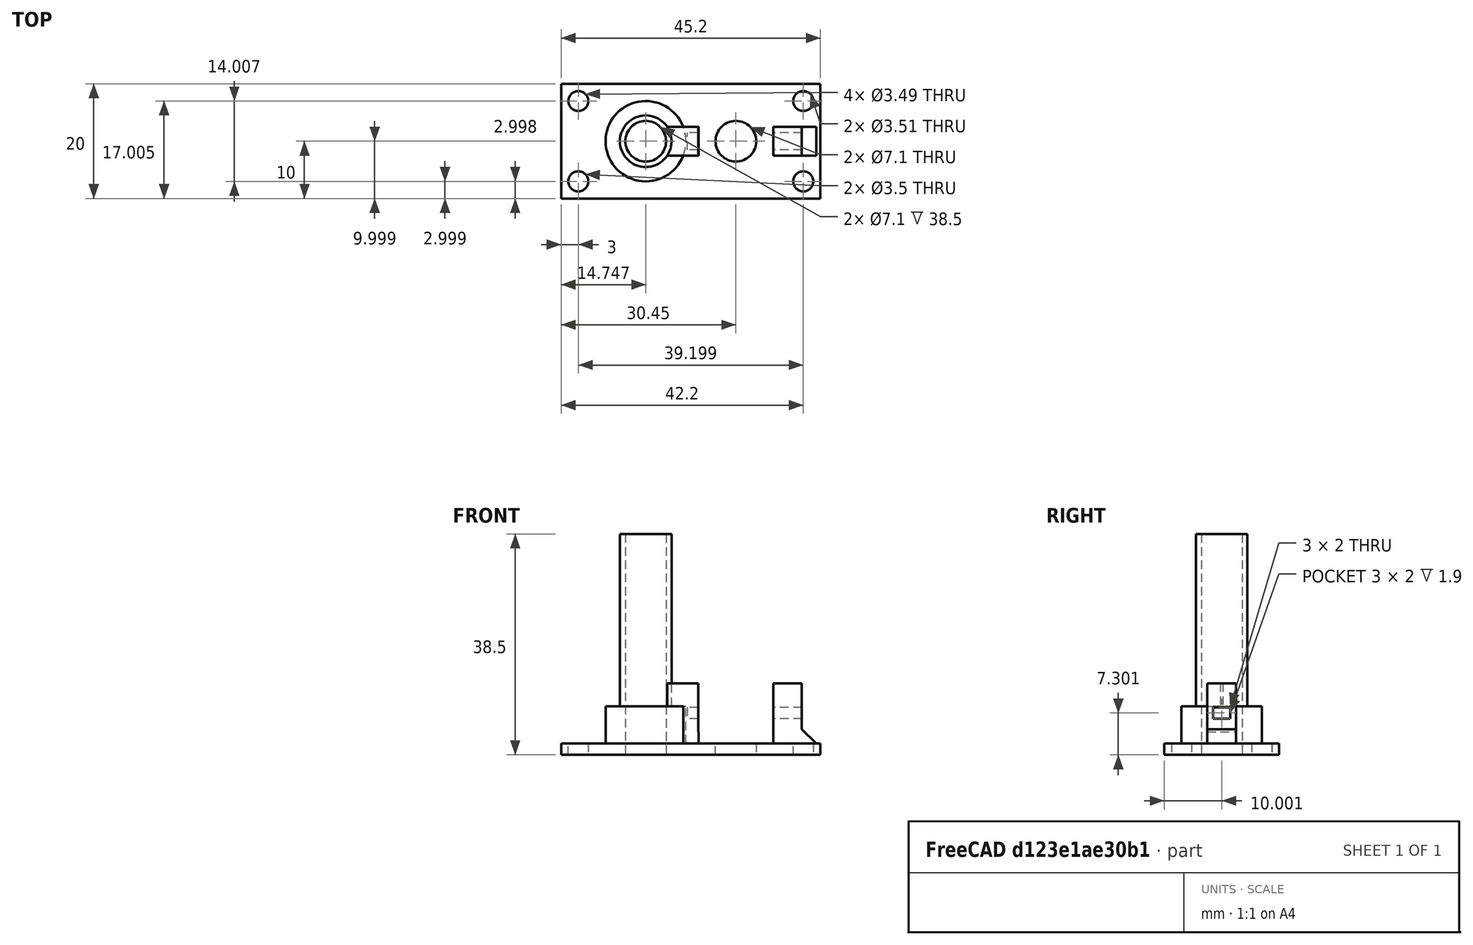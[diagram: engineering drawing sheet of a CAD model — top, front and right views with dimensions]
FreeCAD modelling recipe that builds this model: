
FCSTD DOCUMENT  (FreeCAD 0.17R13522 (Git))
Label: base_media_con_soportes_v3
License: CreativeCommons Attribution-ShareAlike
LicenseURL: http://creativecommons.org/licenses/by-sa/4.0/
objects: Part::Extrusion×15, Part::Part2DObjectPython×13, Part::Cut×13, Part::Fuse×10, Part::Feature×5, Part::Box×2, Part::MultiFuse×1, Part::Chamfer×1
note: 60 computed .brp shape members not serialized (recipe doc carries the construction recipe); baked Part::Feature solids carry a one-line shape summary decoded from their .brp

FEATURE [Part::Box] Box  label="placa base"
  AttacherType = Attacher::AttachEngine3D
  Height = 2
  Length = 45.2
  Width = 20
FEATURE [Part::Part2DObjectPython] Circle  label="taladro inferior izquierdo"  # Draft 2D object (typed FeaturePython)
  FirstAngle = 0
  LastAngle = 0
  MakeFace = false
  Placement = pos=(3,2.99873,2) rot=(0,0,1;3.14159rad)
  Radius = 1.74945
FEATURE [Part::Part2DObjectPython] Circle001  label="taladro inferior derecho"  # Draft 2D object (typed FeaturePython)
  FirstAngle = 0
  LastAngle = 0
  MakeFace = false
  Placement = pos=(42.1991,2.99781,2) rot=(0,0,1;3.14159rad)
  Radius = 1.7464
FEATURE [Part::Part2DObjectPython] Circle002  label="taladro superior derecho"  # Draft 2D object (typed FeaturePython)
  FirstAngle = 0
  LastAngle = 0
  MakeFace = false
  Placement = pos=(42.2,17.005,2) rot=(0,0,1;3.14159rad)
  Radius = 1.75369
FEATURE [Part::Part2DObjectPython] Circle003  label="taladro superior izquierdo"  # Draft 2D object (typed FeaturePython)
  FirstAngle = 0
  LastAngle = 0
  MakeFace = false
  Placement = pos=(3,17.005,2) rot=(0,0,1;3.14159rad)
  Radius = 1.74699
FEATURE [Part::Extrusion] Extrude
  Base = -> Circle003
  Dir = (0,0,1)
  DirMode = 2
  FaceMakerClass = Part::FaceMakerBullseye
  LengthFwd = 10
  LengthRev = 0
  Placement = pos=(0,0,-5) rot=(0,0,1;0rad)
  Solid = true
  Symmetric = false
FEATURE [Part::Extrusion] Extrude001
  Base = -> Circle
  Dir = (0,0,1)
  DirMode = 2
  FaceMakerClass = Part::FaceMakerBullseye
  LengthFwd = 10
  LengthRev = 0
  Placement = pos=(0,0,-5) rot=(0,0,1;0rad)
  Solid = true
  Symmetric = false
FEATURE [Part::Extrusion] Extrude002
  Base = -> Circle001
  Dir = (0,0,1)
  DirMode = 2
  FaceMakerClass = Part::FaceMakerBullseye
  LengthFwd = 10
  LengthRev = 0
  Placement = pos=(0,0,-5) rot=(0,0,1;0rad)
  Solid = true
  Symmetric = false
FEATURE [Part::Extrusion] Extrude003
  Base = -> Circle002
  Dir = (0,0,1)
  DirMode = 2
  FaceMakerClass = Part::FaceMakerBullseye
  LengthFwd = 10
  LengthRev = 0
  Placement = pos=(0,0,-5) rot=(0,0,1;0rad)
  Solid = true
  Symmetric = false
FEATURE [Part::Cut] Cut
  Base = -> Box
  Refine = true
  Tool = -> Extrude001
FEATURE [Part::Cut] Cut001
  Base = -> Cut
  Refine = true
  Tool = -> Extrude
FEATURE [Part::Cut] Cut002
  Base = -> Cut001
  Refine = true
  Tool = -> Extrude002
FEATURE [Part::Cut] Cut003  label="base con taladros en esquina"
  Base = -> Cut002
  Refine = true
  Tool = -> Extrude003
FEATURE [Part::Part2DObjectPython] Circle004  # Draft 2D object (typed FeaturePython)
  FirstAngle = 0
  LastAngle = 0
  MakeFace = false
  Placement = pos=(30.45,10,2) rot=(0,0,1;3.14159rad)
  Radius = 3.55
FEATURE [Part::Extrusion] Extrude004
  Base = -> Circle004
  Dir = (0,0,1)
  DirMode = 2
  FaceMakerClass = Part::FaceMakerBullseye
  LengthFwd = 10
  LengthRev = 0
  Placement = pos=(0,0,-4) rot=(0,0,1;0rad)
  Solid = true
  Symmetric = false
FEATURE [Part::Cut] Cut004  label="base con agujeros"
  Base = -> Cut003
  Refine = true
  Tool = -> Extrude004
FEATURE [Part::Feature] Cut004_solid001001  label="base con agujeros (Solid)002"
  shape: bbox 45.2 x 20 x 2 mm, 11 faces (baked)
FEATURE [Part::Part2DObjectPython] Circle005  # Draft 2D object (typed FeaturePython)
  FirstAngle = 0
  LastAngle = 0
  MakeFace = false
  Placement = pos=(14.7474,9.99931,2) rot=(0,0,1;0rad)
  Radius = 3.55
FEATURE [Part::Part2DObjectPython] Circle006  # Draft 2D object (typed FeaturePython)
  FirstAngle = 0
  LastAngle = 0
  MakeFace = false
  Placement = pos=(14.7474,9.99931,2) rot=(0,0,1;0rad)
  Radius = 4.5
  Support = -> [Cut004_solid001001]
FEATURE [Part::Part2DObjectPython] Circle007  # Draft 2D object (typed FeaturePython)
  FirstAngle = 0
  LastAngle = 0
  MakeFace = false
  Placement = pos=(14.7474,9.99931,2) rot=(0,0,1;0rad)
  Radius = 7
FEATURE [Part::Extrusion] Extrude005
  Base = -> Circle005
  Dir = (0,0,1)
  DirMode = 2
  FaceMakerClass = Part::FaceMakerBullseye
  LengthFwd = 50
  LengthRev = 0
  Solid = true
  Symmetric = false
FEATURE [Part::Extrusion] Extrude006
  Base = -> Circle006
  Dir = (0,0,1)
  DirMode = 2
  FaceMakerClass = Part::FaceMakerBullseye
  LengthFwd = 36.5
  LengthRev = 0
  Solid = true
  Symmetric = false
FEATURE [Part::Extrusion] Extrude007
  Base = -> Circle007
  Dir = (0,0,1)
  DirMode = 2
  FaceMakerClass = Part::FaceMakerBullseye
  LengthFwd = 6.5
  LengthRev = 0
  Solid = true
  Symmetric = false
FEATURE [Part::MultiFuse] Fusion
  Refine = true
  Shapes = -> [Cut004_solid001001,Extrude007,Extrude006]
FEATURE [Part::Cut] Cut005
  Base = -> Fusion
  Refine = true
  Tool = -> Extrude005
FEATURE [Part::Part2DObjectPython] Circle008  # Draft 2D object (typed FeaturePython)
  FirstAngle = 0
  LastAngle = 0
  MakeFace = false
  Placement = pos=(14.7474,9.99931,2) rot=(0,0,1;0rad)
  Radius = 3.55
FEATURE [Part::Extrusion] Extrude008
  Base = -> Circle008
  Dir = (0,0,1)
  DirMode = 2
  FaceMakerClass = Part::FaceMakerBullseye
  LengthFwd = 50
  LengthRev = 0
  Placement = pos=(0,0,-7) rot=(0,0,1;0rad)
  Solid = true
  Symmetric = false
FEATURE [Part::Cut] Cut006
  Base = -> Cut005
  Refine = true
  Tool = -> Extrude008
FEATURE [Part::Feature] Clone002
  Placement = pos=(22.6,10,-1.5) rot=(0,0,1;0rad)
  shape: bbox 6 x 5 x 8 mm, 10 faces (baked)
FEATURE [Part::Feature] Clone001001  label="Clone003"
  Placement = pos=(38.3,10,9.927e-05) rot=(0,0,1;0rad)
  shape: bbox 6 x 5 x 8 mm, 10 faces (baked)
FEATURE [Part::Fuse] Fusion001
  Base = -> Extrude007
  Refine = true
  Tool = -> Clone002
FEATURE [Part::Cut] Cut007
  Base = -> Cut004
  Refine = true
  Tool = -> Extrude008
FEATURE [Part::Fuse] Fusion002
  Base = -> Clone001001
  Refine = true
  Tool = -> Cut007
FEATURE [Part::Chamfer] Chamfer
  Base = -> Fusion002
  Edges = 1 edges r=2.5: [Edge24]
FEATURE [Part::Cut] Cut008
  Base = -> Fusion
  Refine = true
  Tool = -> Extrude005
FEATURE [Part::Fuse] Fusion003
  Base = -> Fusion001
  Refine = true
  Tool = -> Chamfer
FEATURE [Part::Fuse] Fusion004
  Base = -> Cut008
  Refine = true
  Tool = -> Fusion003
FEATURE [Part::Cut] Cut009
  Base = -> Fusion004
  Refine = true
  Tool = -> Extrude008
FEATURE [Part::Part2DObjectPython] Rectangle  # Draft 2D object (typed FeaturePython)
  ChamferSize = 0
  Columns = 1
  FilletRadius = 0
  Height = 1.80868
  Length = 0.123222
  MakeFace = true
  Placement = pos=(23.8348,7.5,6.49553) rot=(1,0,0;1.5708rad)
  Rows = 1
FEATURE [Part::Extrusion] Extrude009
  Base = -> Rectangle
  Dir = (0,-1,0)
  DirMode = 2
  FaceMakerClass = Part::FaceMakerBullseye
  LengthFwd = 5
  LengthRev = 0
  Placement = pos=(0,5,0) rot=(0,0,1;0rad)
  Solid = false
  Symmetric = false
FEATURE [Part::Fuse] Fusion005
  Base = -> Cut009
  Refine = true
  Tool = -> Extrude009
FEATURE [Part::Part2DObjectPython] Rectangle001  # Draft 2D object (typed FeaturePython)
  ChamferSize = 0
  Columns = 1
  FilletRadius = 0
  Height = 1.81025
  Length = 0.139714
  MakeFace = true
  Placement = pos=(36.942,7.5,6.49563) rot=(1,0,0;1.5708rad)
  Rows = 1
FEATURE [Part::Extrusion] Extrude010
  Base = -> Rectangle001
  Dir = (0,-1,0)
  DirMode = 2
  FaceMakerClass = Part::FaceMakerBullseye
  LengthFwd = 5
  LengthRev = 0
  Placement = pos=(0,5,0) rot=(0,0,1;0rad)
  Solid = false
  Symmetric = false
FEATURE [Part::Fuse] Fusion006
  Base = -> Fusion005
  Refine = true
  Tool = -> Extrude010
FEATURE [Part::Box] Box001  label="Cube"
  AttacherType = Attacher::AttachEngine3D
  Height = 11
  Length = 5
  Placement = pos=(23.9,5,4) rot=(0,0,1;0rad)
  Width = 10
FEATURE [Part::Feature] Box001001  label="Cube001"
  Placement = pos=(32,5,4) rot=(0,0,1;0rad)
  shape: bbox 5 x 10 x 11 mm, 6 faces (baked)
FEATURE [Part::Cut] Cut010
  Base = -> Fusion006
  Refine = true
  Tool = -> Box001001
FEATURE [Part::Cut] Cut011
  Base = -> Cut010
  Refine = true
  Tool = -> Box001
FEATURE [Part::Part2DObjectPython] Rectangle002  # Draft 2D object (typed FeaturePython)
  ChamferSize = 0
  Columns = 1
  FilletRadius = 0
  Height = 4.95
  Length = 5
  MakeFace = true
  Placement = pos=(37,12.5,8.5001) rot=(0,0,-1;1.5708rad)
  Rows = 1
  Support = -> [Cut011]
FEATURE [Part::Extrusion] Extrude011
  Base = -> Rectangle002
  Dir = (0,0,1)
  DirMode = 2
  FaceMakerClass = Part::FaceMakerBullseye
  LengthFwd = 4
  LengthRev = 0
  Solid = false
  Symmetric = false
FEATURE [Part::Extrusion] Extrude012
  Base = -> Rectangle002
  Dir = (0,0,1)
  DirMode = 2
  FaceMakerClass = Part::FaceMakerBullseye
  LengthFwd = 4
  LengthRev = 0
  Solid = false
  Symmetric = false
FEATURE [Part::Part2DObjectPython] Rectangle003  # Draft 2D object (typed FeaturePython)
  ChamferSize = 0
  Columns = 1
  FilletRadius = 0
  Height = 5.61
  Length = 5
  MakeFace = true
  Placement = pos=(18.29,12.5,8.5) rot=(0,0,-1;1.5708rad)
  Rows = 1
FEATURE [Part::Extrusion] Extrude013
  Base = -> Rectangle003
  Dir = (0,0,1)
  DirMode = 2
  FaceMakerClass = Part::FaceMakerBullseye
  LengthFwd = 4
  LengthRev = 0
  Solid = false
  Symmetric = false
FEATURE [Part::Extrusion] Extrude014
  Base = -> Rectangle003
  Dir = (0,0,1)
  DirMode = 2
  FaceMakerClass = Part::FaceMakerBullseye
  LengthFwd = 4
  LengthRev = 0
  Solid = false
  Symmetric = false
FEATURE [Part::Fuse] Fusion007
  Base = -> Cut011
  Refine = true
  Tool = -> Extrude013
FEATURE [Part::Fuse] Fusion008
  Base = -> Extrude014
  Refine = true
  Tool = -> Fusion007
FEATURE [Part::Fuse] Fusion009
  Base = -> Extrude011
  Refine = true
  Tool = -> Fusion008
FEATURE [Part::Fuse] Fusion010
  Base = -> Extrude012
  Refine = true
  Tool = -> Fusion009
FEATURE [Part::Feature] Extrude009001001  label="Extrude015"
  Placement = pos=(3,0,0) rot=(0,0,1;0rad)
  shape: bbox 36 x 3 x 2 mm, 6 faces (baked)
FEATURE [Part::Cut] Cut012
  Base = -> Fusion010
  Refine = true
  Tool = -> Extrude009001001
